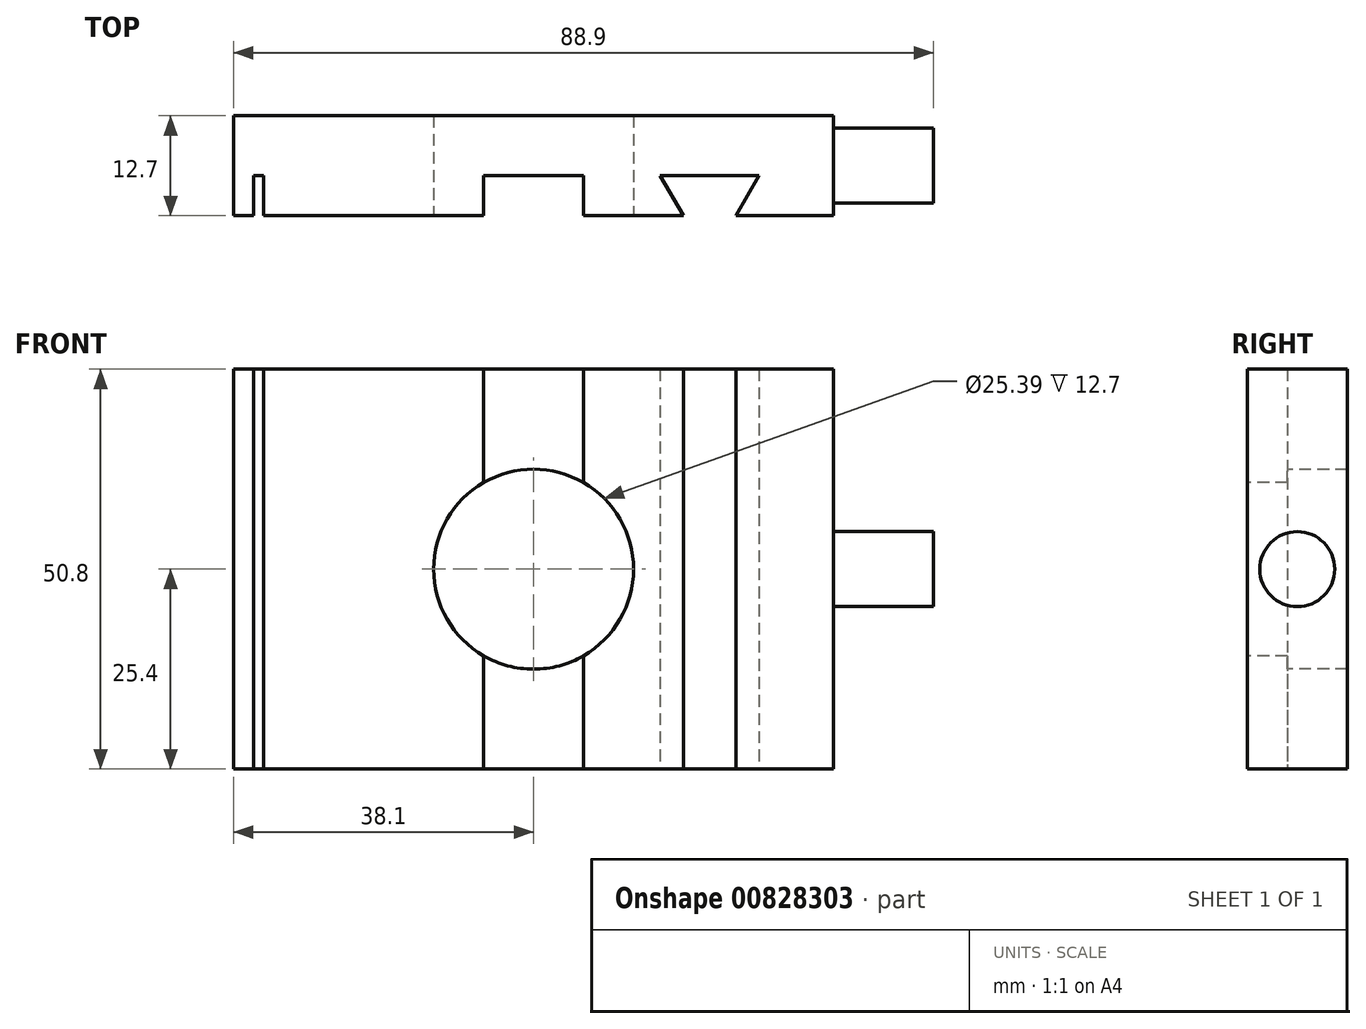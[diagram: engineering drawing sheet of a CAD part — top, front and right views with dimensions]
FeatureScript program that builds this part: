
annotation { "Feature Type Name" : "Feature", "Feature Type Description" : "" }
export const myFeature = defineFeature(function(context is Context, id is Id, definition is map)
    precondition{}
    {
        {
            var Q0;
            Q0=qCreatedBy(makeId("Front.planeOp"),FACE);
            var sketch = newSketch(context, id + "F0", { "sketchPlane" : qUnion([Q0])});
            skLineSegment(sketch, "E0.bottom", {"start": v(38.1, 25.4) * mm, "end": v(-38.1, 25.4) * mm});
            skLineSegment(sketch, "E0.top", {"start": v(38.1, -25.4) * mm, "end": v(-38.1, -25.4) * mm});
            skLineSegment(sketch, "E0.left", {"start": v(38.1, 25.4) * mm, "end": v(38.1, -25.4) * mm});
            skLineSegment(sketch, "E0.right", {"start": v(-38.1, 25.4) * mm, "end": v(-38.1, -25.4) * mm});
            skPoint(sketch, "E0.middle", {"position": v(0, 0) * mm});
            skSolve(sketch);
        }
        {
            var Q0;
            Q0=makeQuery(id+"F0.imprint","IMPRINT",FACE,{"disambiguationData":[TD([[makeQuery(id+"F0.imprint","IMPRINT",EDGE,{"derivedFrom":sQuery(id+"F0.wireOp",EDGE,"E0.bottom")}),1.0]])]});
            extrude(context, id + "F1", {"entities" : qUnion([Q0]), "depth" : 12.7 * mm, "offsetDistance" : 25.4 * mm});
        }
        {
            var Q0;
            Q0=makeQuery(id+"F1.opExtrude","CAP_FACE",FACE,{"disambiguationData":[OSD([sQuery(id+"F0.wireOp",EDGE,"E0.bottom"),sQuery(id+"F0.wireOp",EDGE,"E0.top"),sQuery(id+"F0.wireOp",EDGE,"E0.left"),sQuery(id+"F0.wireOp",EDGE,"E0.right")])],"isStart":false});
            var sketch = newSketch(context, id + "F2", { "sketchPlane" : qUnion([Q0])});
            skLineSegment(sketch, "E1.bottom", {"start": v(-35.56, 25.4) * mm, "end": v(-34.29, 25.4) * mm});
            skLineSegment(sketch, "E1.top", {"start": v(-35.56, -25.4) * mm, "end": v(-34.29, -25.4) * mm});
            skLineSegment(sketch, "E1.left", {"start": v(-35.56, 25.4) * mm, "end": v(-35.56, -25.4) * mm});
            skLineSegment(sketch, "E1.right", {"start": v(-34.29, 25.4) * mm, "end": v(-34.29, -25.4) * mm});
            skCircle(sketch, "E2", {"center": v(0, 0) * mm, "radius": 12.7 * mm});
            skLineSegment(sketch, "E3.bottom", {"start": v(6.35, 25.4) * mm, "end": v(-6.35, 25.4) * mm});
            skLineSegment(sketch, "E3.top", {"start": v(6.35, -25.4) * mm, "end": v(-6.35, -25.4) * mm});
            skLineSegment(sketch, "E3.left", {"start": v(6.35, 25.4) * mm, "end": v(6.35, -25.4) * mm});
            skLineSegment(sketch, "E3.right", {"start": v(-6.35, 25.4) * mm, "end": v(-6.35, -25.4) * mm});
            skSolve(sketch);
        }
        {
            var Q0;
            {var subQ0=sQuery(id+"F2.wireOp",EDGE,"E3.right");var subQ1=sQuery(id+"F2.wireOp",EDGE,"E2");var subQ2=makeQuery(id+"F2.imprint","INTERSECT",VERTEX,{"disambiguationData":[OD(0.0)],"derivedFrom":[subQ1,subQ0]});Q0=makeQuery(id+"F2.imprint","IMPRINT",FACE,{"disambiguationData":[TD([[makeQuery(id+"F2.imprint","IMPRINT",EDGE,{"disambiguationData":[TD([[subQ2,-1.0]])],"derivedFrom":subQ1}),1.0]])]});}
            var Q1;
            {var subQ0=sQuery(id+"F2.wireOp",EDGE,"E3.right");var subQ1=sQuery(id+"F2.wireOp",EDGE,"E2");var subQ2=makeQuery(id+"F2.imprint","INTERSECT",VERTEX,{"disambiguationData":[OD(0.0)],"derivedFrom":[subQ1,subQ0]});Q1=makeQuery(id+"F2.imprint","IMPRINT",FACE,{"disambiguationData":[TD([[makeQuery(id+"F2.imprint","IMPRINT",EDGE,{"disambiguationData":[TD([[subQ2,1.0]])],"derivedFrom":subQ1}),1.0]])]});}
            var Q2;
            {var subQ0=sQuery(id+"F2.wireOp",EDGE,"E3.left");var subQ1=sQuery(id+"F2.wireOp",EDGE,"E2");var subQ2=makeQuery(id+"F2.imprint","INTERSECT",VERTEX,{"disambiguationData":[OD(0.0)],"derivedFrom":[subQ1,subQ0]});Q2=makeQuery(id+"F2.imprint","IMPRINT",FACE,{"disambiguationData":[TD([[makeQuery(id+"F2.imprint","IMPRINT",EDGE,{"disambiguationData":[TD([[subQ2,1.0]])],"derivedFrom":subQ1}),1.0]])]});}
            extrude(context, id + "F3", {"entities" : qUnion([Q0, Q1, Q2]), "operationType" : NewBodyOperationType.REMOVE, "oppositeDirection" : true, "depth" : 12.7 * mm, "offsetDistance" : 25.4 * mm});
        }
        {
            var Q0;
            Q0=qSketchRegion(id+"F2",true);
            extrude(context, id + "F4", {"entities" : qUnion([Q0]), "operationType" : NewBodyOperationType.REMOVE, "oppositeDirection" : true, "depth" : 5.08 * mm, "offsetDistance" : 25.4 * mm});
        }
        {
            var Q0;
            Q0=makeQuery(id+"F1.opExtrude","SWEPT_FACE",FACE,{"disambiguationData":[OSD([sQuery(id+"F0.wireOp",EDGE,"E0.top")])]});
            var sketch = newSketch(context, id + "F5", { "sketchPlane" : qUnion([Q0])});
            skLineSegment(sketch, "E4", {"start": v(19.02, 12.7) * mm, "end": v(16.09, 7.62) * mm});
            skLineSegment(sketch, "E5", {"start": v(28.64, 7.62) * mm, "end": v(25.7, 12.7) * mm});
            skLineSegment(sketch, "E6", {"start": v(25.7, 12.7) * mm, "end": v(19.02, 12.7) * mm});
            skLineSegment(sketch, "E7", {"start": v(16.09, 7.62) * mm, "end": v(28.64, 7.62) * mm});
            skSolve(sketch);
        }
        {
            var Q0;
            Q0=qSketchRegion(id+"F5",true);
            extrude(context, id + "F6", {"entities" : qUnion([Q0]), "operationType" : NewBodyOperationType.REMOVE, "oppositeDirection" : true, "depth" : 50.8 * mm, "offsetDistance" : 25.4 * mm});
        }
        {
            var Q0;
            Q0=makeQuery(id+"F1.opExtrude","SWEPT_FACE",FACE,{"disambiguationData":[OSD([sQuery(id+"F0.wireOp",EDGE,"E0.left")])]});
            var sketch = newSketch(context, id + "F7", { "sketchPlane" : qUnion([Q0])});
            skCircle(sketch, "E8", {"center": v(-6.35, 0) * mm, "radius": 4.76 * mm});
            skPoint(sketch, "E8.centerSnap0", {"position": v(-12.7, 0) * mm});
            skPoint(sketch, "E8.centerSnap1", {"position": v(-6.35, -25.4) * mm});
            skSolve(sketch);
        }
        {
            var Q0;
            Q0=makeQuery(id+"F7.imprint","IMPRINT",FACE,{"disambiguationData":[TD([[makeQuery(id+"F7.imprint","IMPRINT",EDGE,{"derivedFrom":sQuery(id+"F7.wireOp",EDGE,"E8")}),1.0]])]});
            extrude(context, id + "F8", {"entities" : qUnion([Q0]), "operationType" : NewBodyOperationType.ADD, "depth" : 12.7 * mm, "offsetDistance" : 25.4 * mm});
        }
    });
